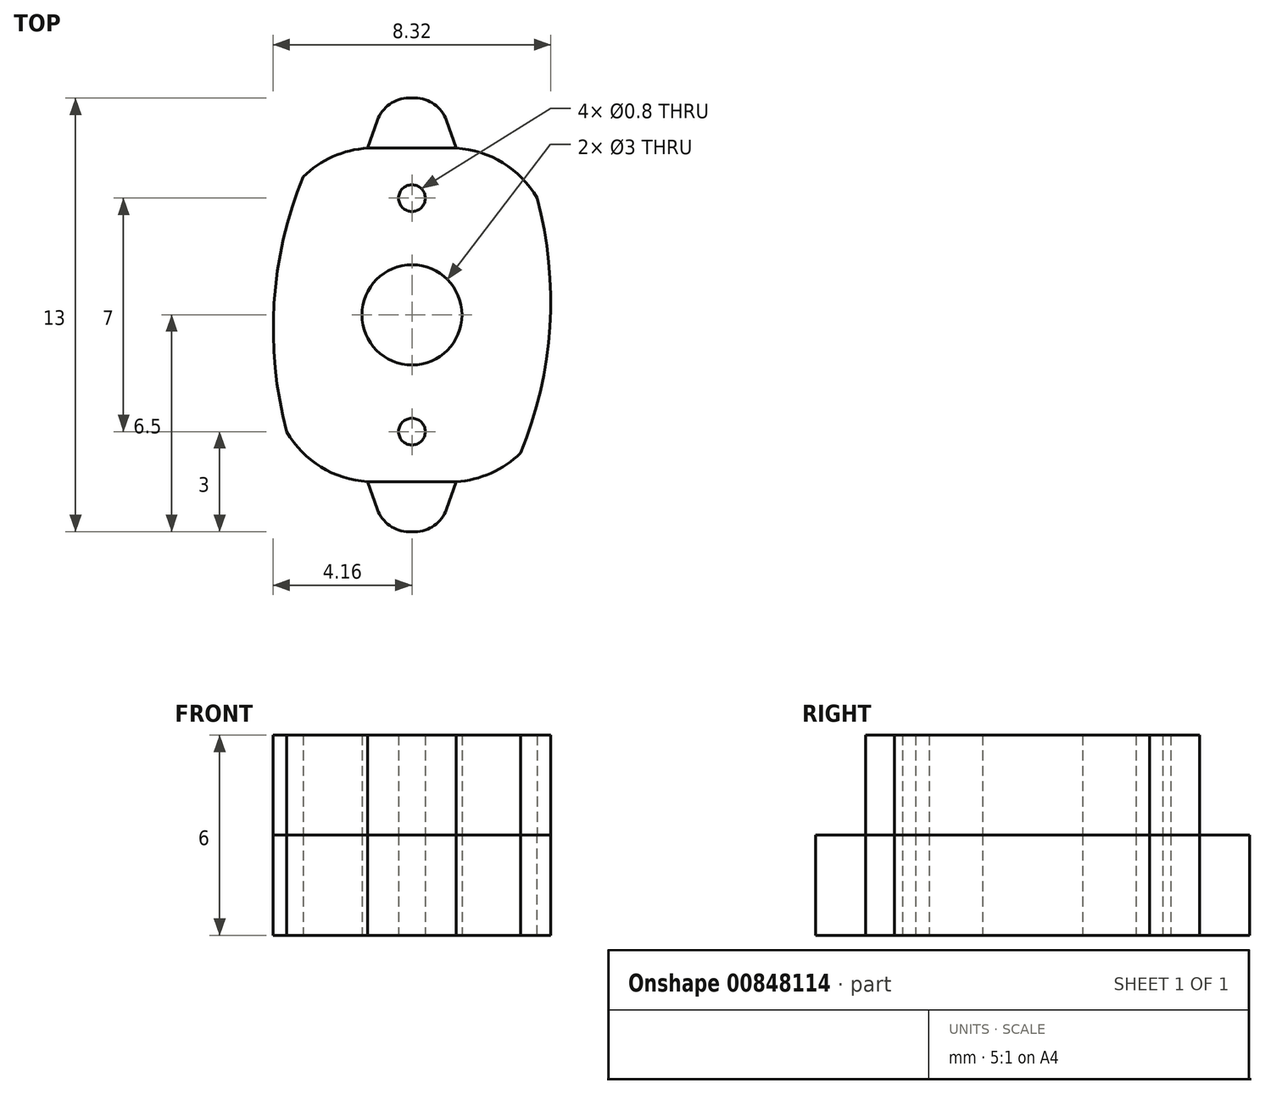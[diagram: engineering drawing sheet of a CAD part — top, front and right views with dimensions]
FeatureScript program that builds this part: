
annotation { "Feature Type Name" : "Feature", "Feature Type Description" : "" }
export const myFeature = defineFeature(function(context is Context, id is Id, definition is map)
    precondition{}
    {
        {
            var Q0;
            Q0=qCreatedBy(makeId("Top.planeOp"),FACE);
            var sketch = newSketch(context, id + "F0", { "sketchPlane" : qUnion([Q0])});
            skCircle(sketch, "E0.cCircle", {"center": v(0, 0) * mm, "radius": 5 * mm, "construction": true});
            skLineSegment(sketch, "E0.0", {"start": v(-2.89, 5) * mm, "end": v(2.89, 5) * mm});
            skLineSegment(sketch, "E0.1", {"start": v(2.89, 5) * mm, "end": v(5.77, 0) * mm});
            skLineSegment(sketch, "E0.2", {"start": v(5.77, 0) * mm, "end": v(2.89, -5) * mm});
            skLineSegment(sketch, "E0.3", {"start": v(2.89, -5) * mm, "end": v(-2.89, -5) * mm});
            skLineSegment(sketch, "E0.4", {"start": v(-2.89, -5) * mm, "end": v(-5.77, 0) * mm});
            skLineSegment(sketch, "E0.5", {"start": v(-5.77, 0) * mm, "end": v(-2.89, 5) * mm});
            skPoint(sketch, "E0.0.midPoint", {"position": v(0, 5) * mm});
            skLineSegment(sketch, "E1.bottom", {"start": v(1.5, 6.5) * mm, "end": v(-1.5, 6.5) * mm});
            skLineSegment(sketch, "E1.top", {"start": v(1.5, -6.5) * mm, "end": v(-1.5, -6.5) * mm});
            skLineSegment(sketch, "E1.left", {"start": v(1.5, 6.5) * mm, "end": v(1.5, -6.5) * mm});
            skLineSegment(sketch, "E1.right", {"start": v(-1.5, 6.5) * mm, "end": v(-1.5, -6.5) * mm});
            skCircle(sketch, "E2", {"center": v(0, 0) * mm, "radius": 1.5 * mm});
            skCircle(sketch, "E3", {"center": v(0, 3.5) * mm, "radius": 0.4 * mm});
            skLineSegment(sketch, "E4", {"start": v(0, 0) * mm, "end": v(-5.77, 0) * mm, "construction": true});
            skCircle(sketch, "E5.MirrorC", {"center": v(0, -3.5) * mm, "radius": 0.4 * mm});
            skSolve(sketch);
        }
        {
            var Q0;
            {var subQ1=sQuery(id+"F0.wireOp",EDGE,"dec11852-9c37-43c0-9047-43a356c926e4.4");Q0=makeQuery(id+"F0.imprint","IMPRINT",FACE,{"disambiguationData":[TD([[makeQuery(id+"F0.imprint","IMPRINT",EDGE,{"derivedFrom":subQ1}),1.0]])]});}
            var Q1;
            {var subQ0=sQuery(id+"F0.wireOp",EDGE,"E1.right");var subQ1=sQuery(id+"F0.wireOp",EDGE,"dec11852-9c37-43c0-9047-43a356c926e4.0");var subQ2=makeQuery(id+"F0.imprint","INTERSECT",VERTEX,{"derivedFrom":[subQ1,subQ0]});Q1=makeQuery(id+"F0.imprint","IMPRINT",FACE,{"disambiguationData":[TD([[makeQuery(id+"F0.imprint","IMPRINT",EDGE,{"disambiguationData":[TD([[subQ2,-1.0]])],"derivedFrom":subQ1}),1.0]])]});}
            var Q2;
            {var subQ7=sQuery(id+"F0.wireOp",EDGE,"dec11852-9c37-43c0-9047-43a356c926e4.1");Q2=makeQuery(id+"F0.imprint","IMPRINT",FACE,{"disambiguationData":[TD([[makeQuery(id+"F0.imprint","IMPRINT",EDGE,{"derivedFrom":subQ7}),1.0]])]});}
            var Q3;
            {var subQ0=sQuery(id+"F0.wireOp",EDGE,"E1.left");var subQ1=sQuery(id+"F0.wireOp",EDGE,"dec11852-9c37-43c0-9047-43a356c926e4.3");var subQ2=makeQuery(id+"F0.imprint","INTERSECT",VERTEX,{"derivedFrom":[subQ1,subQ0]});Q3=makeQuery(id+"F0.imprint","IMPRINT",FACE,{"disambiguationData":[TD([[makeQuery(id+"F0.imprint","IMPRINT",EDGE,{"disambiguationData":[TD([[subQ2,-1.0]])],"derivedFrom":subQ1}),1.0]])]});}
            var Q4;
            {var subQ5=sQuery(id+"F0.wireOp",EDGE,"E1.bottom");Q4=makeQuery(id+"F0.imprint","IMPRINT",FACE,{"disambiguationData":[TD([[makeQuery(id+"F0.imprint","IMPRINT",EDGE,{"derivedFrom":subQ5}),1.0]])]});}
            var Q5;
            {var subQ1=sQuery(id+"F0.wireOp",EDGE,"E0.4");Q5=makeQuery(id+"F0.imprint","IMPRINT",FACE,{"disambiguationData":[TD([[makeQuery(id+"F0.imprint","IMPRINT",EDGE,{"derivedFrom":subQ1}),-1.0]])]});}
            var Q6;
            {var subQ0=sQuery(id+"F0.wireOp",EDGE,"E1.right");var subQ1=sQuery(id+"F0.wireOp",EDGE,"E0.0");var subQ2=makeQuery(id+"F0.imprint","INTERSECT",VERTEX,{"derivedFrom":[subQ1,subQ0]});Q6=makeQuery(id+"F0.imprint","IMPRINT",FACE,{"disambiguationData":[TD([[makeQuery(id+"F0.imprint","IMPRINT",EDGE,{"disambiguationData":[TD([[subQ2,-1.0]])],"derivedFrom":subQ1}),-1.0]])]});}
            var Q7;
            {var subQ0=sQuery(id+"F0.wireOp",EDGE,"E1.left");var subQ1=sQuery(id+"F0.wireOp",EDGE,"E0.3");var subQ2=makeQuery(id+"F0.imprint","INTERSECT",VERTEX,{"derivedFrom":[subQ1,subQ0]});Q7=makeQuery(id+"F0.imprint","IMPRINT",FACE,{"disambiguationData":[TD([[makeQuery(id+"F0.imprint","IMPRINT",EDGE,{"disambiguationData":[TD([[subQ2,-1.0]])],"derivedFrom":subQ1}),-1.0]])]});}
            var Q8;
            {var subQ4=sQuery(id+"F0.wireOp",EDGE,"E0.1");Q8=makeQuery(id+"F0.imprint","IMPRINT",FACE,{"disambiguationData":[TD([[makeQuery(id+"F0.imprint","IMPRINT",EDGE,{"derivedFrom":subQ4}),-1.0]])]});}
            extrude(context, id + "F1", {"entities" : qUnion([Q0, Q1, Q2, Q3, Q4, Q5, Q6, Q7, Q8]), "depth" : 3 * mm, "offsetDistance" : 25 * mm});
        }
        {
            var Q0;
            Q0=makeQuery(id+"F1.opExtrude","SWEPT_EDGE",EDGE,{"disambiguationData":[OSD([sQuery(id+"F0.wireOp",EDGE,"E1.bottom"),sQuery(id+"F0.wireOp",EDGE,"E1.right")])]});
            var Q1;
            Q1=makeQuery(id+"F1.opExtrude","SWEPT_EDGE",EDGE,{"disambiguationData":[OSD([sQuery(id+"F0.wireOp",EDGE,"E1.bottom"),sQuery(id+"F0.wireOp",EDGE,"E1.left")])]});
            chamfer(context, id + "F2", {"entities" : qUnion([Q0, Q1]), "chamferType" : ChamferType.TWO_OFFSETS, "width1" : 0.7 * mm, "oppositeDirection" : true, "width2" : 2 * mm});
        }
        {
            var Q0;
            Q0=makeQuery(id+"F1.opExtrude","SWEPT_BODY",BODY,{"disambiguationData":[OSD([sQuery(id+"F0.wireOp",EDGE,"dec11852-9c37-43c0-9047-43a356c926e4.0"),sQuery(id+"F0.wireOp",EDGE,"dec11852-9c37-43c0-9047-43a356c926e4.1"),sQuery(id+"F0.wireOp",EDGE,"dec11852-9c37-43c0-9047-43a356c926e4.2"),sQuery(id+"F0.wireOp",EDGE,"dec11852-9c37-43c0-9047-43a356c926e4.3"),sQuery(id+"F0.wireOp",EDGE,"dec11852-9c37-43c0-9047-43a356c926e4.4"),sQuery(id+"F0.wireOp",EDGE,"dec11852-9c37-43c0-9047-43a356c926e4.5"),sQuery(id+"F0.wireOp",EDGE,"E0.0"),sQuery(id+"F0.wireOp",EDGE,"E0.1"),sQuery(id+"F0.wireOp",EDGE,"E0.2"),sQuery(id+"F0.wireOp",EDGE,"E0.3"),sQuery(id+"F0.wireOp",EDGE,"E0.4"),sQuery(id+"F0.wireOp",EDGE,"E0.5"),sQuery(id+"F0.wireOp",EDGE,"E1.bottom"),sQuery(id+"F0.wireOp",EDGE,"E1.left"),sQuery(id+"F0.wireOp",EDGE,"E1.right")])]});
            var Q1;
            Q1=qCreatedBy(makeId("Front.planeOp"),FACE);
            mirror(context, id + "F3", {"operationType" : NewBodyOperationType.ADD, "entities" : qUnion([Q0]), "mirrorPlane" : qUnion([Q1])});
        }
        {
            var Q0;
            Q0=makeQuery(id+"F1.opExtrude","SWEPT_EDGE",EDGE,{"disambiguationData":[OSD([sQuery(id+"F0.wireOp",EDGE,"E0.0"),sQuery(id+"F0.wireOp",EDGE,"E0.5")])]});
            var Q1;
            Q1=makeQuery(id+"F1.opExtrude","SWEPT_EDGE",EDGE,{"disambiguationData":[OSD([sQuery(id+"F0.wireOp",EDGE,"E0.0"),sQuery(id+"F0.wireOp",EDGE,"E0.1")])]});
            var Q2;
            Q2=makeQuery(id+"F1.opExtrude","SWEPT_EDGE",EDGE,{"disambiguationData":[OSD([sQuery(id+"F0.wireOp",EDGE,"E0.3"),sQuery(id+"F0.wireOp",EDGE,"E0.4")])]});
            var Q3;
            Q3=makeQuery(id+"F1.opExtrude","SWEPT_EDGE",EDGE,{"disambiguationData":[OSD([sQuery(id+"F0.wireOp",EDGE,"E0.2"),sQuery(id+"F0.wireOp",EDGE,"E0.3")])]});
            fillet(context, id + "F4", {"entities" : qUnion([Q0, Q1, Q2, Q3]), "radius" : 3 * mm, "tangentPropagation" : true, "allowEdgeOverflow" : false});
        }
        {
            var Q0;
            {var subQ0=sQuery(id+"F0.wireOp",EDGE,"E1.bottom");Q0=makeQuery(id+"F3.opPattern","COPY",EDGE,{"derivedFrom":makeQuery(id+"F2.opChamfer","BLEND_EDGE",EDGE,{"blendedFrom":[makeQuery(id+"F1.opExtrude","SWEPT_EDGE",EDGE,{"disambiguationData":[OSD([subQ0,sQuery(id+"F0.wireOp",EDGE,"E1.right")])]}),makeQuery(id+"F1.opExtrude","SWEPT_FACE",FACE,{"disambiguationData":[OSD([subQ0])]})],"blendedInto":[makeQuery(id+"F1.opExtrude","SWEPT_FACE",FACE,{"disambiguationData":[OSD([subQ0])]})]}),"instanceName":"1"});}
            var Q1;
            {var subQ0=sQuery(id+"F0.wireOp",EDGE,"E1.bottom");Q1=makeQuery(id+"F3.opPattern","COPY",EDGE,{"derivedFrom":makeQuery(id+"F2.opChamfer","BLEND_EDGE",EDGE,{"blendedFrom":[makeQuery(id+"F1.opExtrude","SWEPT_EDGE",EDGE,{"disambiguationData":[OSD([subQ0,sQuery(id+"F0.wireOp",EDGE,"E1.left")])]}),makeQuery(id+"F1.opExtrude","SWEPT_FACE",FACE,{"disambiguationData":[OSD([subQ0])]})],"blendedInto":[makeQuery(id+"F1.opExtrude","SWEPT_FACE",FACE,{"disambiguationData":[OSD([subQ0])]})]}),"instanceName":"1"});}
            var Q2;
            {var subQ0=sQuery(id+"F0.wireOp",EDGE,"E1.bottom");Q2=makeQuery(id+"F2.opChamfer","BLEND_EDGE",EDGE,{"blendedFrom":[makeQuery(id+"F1.opExtrude","SWEPT_EDGE",EDGE,{"disambiguationData":[OSD([subQ0,sQuery(id+"F0.wireOp",EDGE,"E1.left")])]}),makeQuery(id+"F1.opExtrude","SWEPT_FACE",FACE,{"disambiguationData":[OSD([subQ0])]})],"blendedInto":[makeQuery(id+"F1.opExtrude","SWEPT_FACE",FACE,{"disambiguationData":[OSD([subQ0])]})]});}
            var Q3;
            {var subQ0=sQuery(id+"F0.wireOp",EDGE,"E1.bottom");Q3=makeQuery(id+"F2.opChamfer","BLEND_EDGE",EDGE,{"blendedFrom":[makeQuery(id+"F1.opExtrude","SWEPT_EDGE",EDGE,{"disambiguationData":[OSD([subQ0,sQuery(id+"F0.wireOp",EDGE,"E1.right")])]}),makeQuery(id+"F1.opExtrude","SWEPT_FACE",FACE,{"disambiguationData":[OSD([subQ0])]})],"blendedInto":[makeQuery(id+"F1.opExtrude","SWEPT_FACE",FACE,{"disambiguationData":[OSD([subQ0])]})]});}
            fillet(context, id + "F5", {"entities" : qUnion([Q0, Q1, Q2, Q3]), "radius" : 1 * mm, "tangentPropagation" : true, "allowEdgeOverflow" : false});
        }
        {
            var Q0;
            Q0=makeQuery(id+"F1.opExtrude","SWEPT_EDGE",EDGE,{"disambiguationData":[OSD([sQuery(id+"F0.wireOp",EDGE,"E0.4"),sQuery(id+"F0.wireOp",EDGE,"E0.5")])]});
            var Q1;
            Q1=makeQuery(id+"F1.opExtrude","SWEPT_EDGE",EDGE,{"disambiguationData":[OSD([sQuery(id+"F0.wireOp",EDGE,"E0.1"),sQuery(id+"F0.wireOp",EDGE,"E0.2")])]});
            fillet(context, id + "F6", {"entities" : qUnion([Q0, Q1]), "radius" : 12 * mm, "tangentPropagation" : true, "allowEdgeOverflow" : false});
        }
        {
            var Q0;
            {var subQ0=makeQuery(id+"F1.opExtrude","CAP_FACE",FACE,{"disambiguationData":[OSD([sQuery(id+"F0.wireOp",EDGE,"E0.0"),sQuery(id+"F0.wireOp",EDGE,"E0.1"),sQuery(id+"F0.wireOp",EDGE,"E0.2"),sQuery(id+"F0.wireOp",EDGE,"E0.3"),sQuery(id+"F0.wireOp",EDGE,"E0.4"),sQuery(id+"F0.wireOp",EDGE,"E0.5"),sQuery(id+"F0.wireOp",EDGE,"E1.bottom"),sQuery(id+"F0.wireOp",EDGE,"E1.left"),sQuery(id+"F0.wireOp",EDGE,"E1.right"),sQuery(id+"F0.wireOp",EDGE,"E2")])],"isStart":false});Q0=makeQuery(id+"F3.boolean.opBoolean","MERGE",FACE,{"derivedFrom":[subQ0,makeQuery(id+"F3.opPattern","COPY",FACE,{"derivedFrom":subQ0,"instanceName":"1"})]});}
            var sketch = newSketch(context, id + "F7", { "sketchPlane" : qUnion([Q0])});
            skLineSegment(sketch, "E6", {"start": v(-1.33, 5) * mm, "end": v(1.33, 5) * mm});
            skLineSegment(sketch, "E7", {"start": v(-1.33, -5) * mm, "end": v(1.33, -5) * mm});
            skSolve(sketch);
        }
        {
            var Q0;
            Q0=makeQuery(id+"F7.imprint","IMPRINT",FACE,{"disambiguationData":[TD([[makeQuery(id+"F7.imprint","IMPRINT",EDGE,{"derivedFrom":sQuery(id+"F7.wireOp",EDGE,"E6")}),-1.0]])]});
            extrude(context, id + "F8", {"entities" : qUnion([Q0]), "depth" : 3 * mm, "offsetDistance" : 25 * mm});
        }
    });
